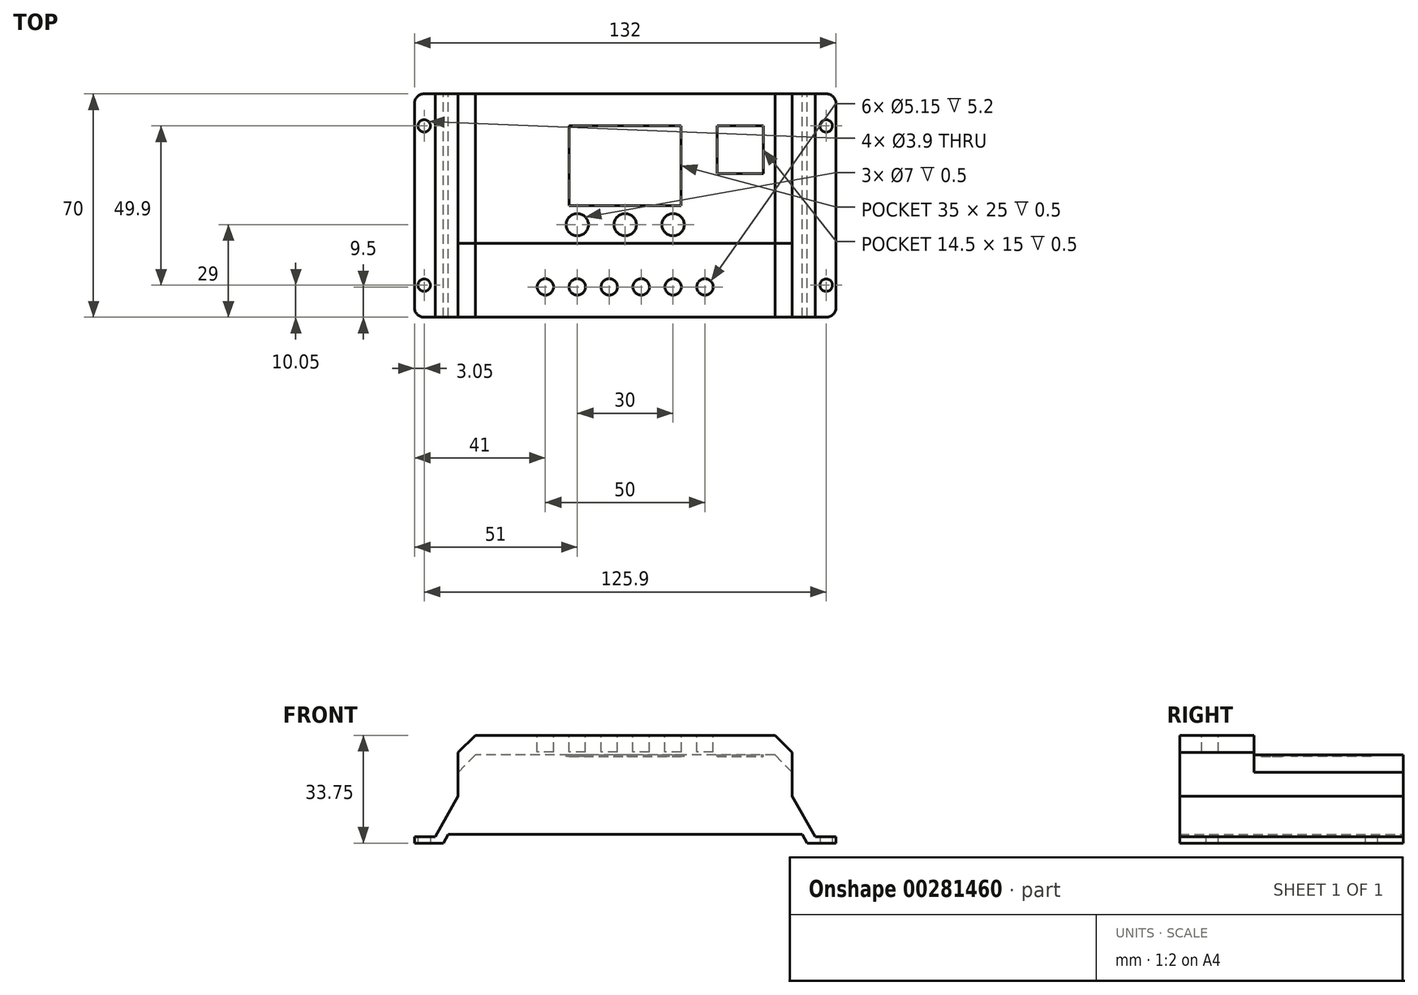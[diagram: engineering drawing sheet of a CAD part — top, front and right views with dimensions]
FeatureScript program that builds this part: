
annotation { "Feature Type Name" : "Feature", "Feature Type Description" : "" }
export const myFeature = defineFeature(function(context is Context, id is Id, definition is map)
    precondition{}
    {
        {
            var Q0;
            Q0=qCreatedBy(makeId("Top.planeOp"),FACE);
            var sketch = newSketch(context, id + "F0", { "sketchPlane" : qUnion([Q0])});
            skLineSegment(sketch, "E0.bottom", {"start": v(-66, 35) * mm, "end": v(66, 35) * mm});
            skLineSegment(sketch, "E0.top", {"start": v(-66, -35) * mm, "end": v(66, -35) * mm});
            skLineSegment(sketch, "E0.left", {"start": v(-66, 35) * mm, "end": v(-66, -35) * mm});
            skLineSegment(sketch, "E0.right", {"start": v(66, 35) * mm, "end": v(66, -35) * mm});
            skPoint(sketch, "E0.middle", {"position": v(0, 0) * mm});
            skSolve(sketch);
        }
        {
            var Q0;
            Q0=makeQuery(id+"F0.imprint","IMPRINT",FACE,{"disambiguationData":[TD([[makeQuery(id+"F0.imprint","IMPRINT",EDGE,{"derivedFrom":sQuery(id+"F0.wireOp",EDGE,"E0.bottom")}),-1.0]])]});
            extrude(context, id + "F1", {"entities" : qUnion([Q0]), "depth" : 2 * mm});
        }
        {
            var Q0;
            Q0=qCreatedBy(makeId("Front.planeOp"),FACE);
            var sketch = newSketch(context, id + "F2", { "sketchPlane" : qUnion([Q0])});
            skLineSegment(sketch, "E1", {"start": v(-59.5, 2) * mm, "end": v(-52.3, 14.7) * mm});
            skLineSegment(sketch, "E2", {"start": v(-52.3, 14.7) * mm, "end": v(-52.3, 22.2) * mm});
            skLineSegment(sketch, "E3", {"start": v(-52.3, 22.2) * mm, "end": v(-46.9, 27.6) * mm});
            skLineSegment(sketch, "E4", {"start": v(-46.9, 27.6) * mm, "end": v(46.9, 27.6) * mm});
            skLineSegment(sketch, "E5", {"start": v(46.9, 27.6) * mm, "end": v(52.3, 22.2) * mm});
            skLineSegment(sketch, "E6", {"start": v(52.3, 22.2) * mm, "end": v(52.3, 14.7) * mm});
            skLineSegment(sketch, "E7", {"start": v(52.3, 14.7) * mm, "end": v(59.5, 2) * mm});
            skLineSegment(sketch, "E8", {"start": v(59.5, 2) * mm, "end": v(-59.5, 2) * mm});
            skLineSegment(sketch, "E9", {"start": v(0, 27.6) * mm, "end": v(0, 0) * mm, "construction": true});
            skSolve(sketch);
        }
        {
            var Q0;
            Q0 = qSketchRegion(id + "F2", true);
            var Q1;
            Q1=makeQuery(id+"F1.opExtrude","SWEPT_FACE",FACE,{"disambiguationData":[OSD([sQuery(id+"F0.wireOp",EDGE,"E0.top")])]});
            extrude(context, id + "F3", {"entities" : qUnion([Q0]), "operationType" : NewBodyOperationType.ADD, "endBound" : BoundingType.UP_TO_SURFACE, "endBoundEntityFace" : qUnion([Q1]), "depth" : 25 * mm});
        }
        {
            var Q0;
            Q0 = qSketchRegion(id + "F2", true);
            var Q1;
            Q1=makeQuery(id+"F1.opExtrude","SWEPT_FACE",FACE,{"disambiguationData":[OSD([sQuery(id+"F0.wireOp",EDGE,"E0.bottom")])]});
            extrude(context, id + "F4", {"entities" : qUnion([Q0]), "operationType" : NewBodyOperationType.ADD, "endBound" : BoundingType.UP_TO_SURFACE, "oppositeDirection" : true, "endBoundEntityFace" : qUnion([Q1]), "depth" : 25 * mm});
        }
        {
            var Q0;
            {var subQ0=sQuery(id+"F0.wireOp",EDGE,"E0.top");Q0=makeQuery(id+"F3.boolean.opBoolean","MERGE",FACE,{"derivedFrom":[makeQuery(id+"F1.opExtrude","SWEPT_FACE",FACE,{"disambiguationData":[OSD([subQ0])]}),makeQuery(id+"F3.opExtrude","CAP_FACE",FACE,{"disambiguationData":[OSD([subQ0])],"isStart":false})]});}
            var sketch = newSketch(context, id + "F5", { "sketchPlane" : qUnion([Q0])});
            skLineSegment(sketch, "E10", {"start": v(-52.3, 22.2) * mm, "end": v(-52.3, 28.35) * mm});
            skLineSegment(sketch, "E11", {"start": v(-52.3, 28.35) * mm, "end": v(-46.9, 33.75) * mm});
            skLineSegment(sketch, "E12", {"start": v(-46.9, 33.75) * mm, "end": v(46.9, 33.75) * mm});
            skLineSegment(sketch, "E13", {"start": v(46.9, 33.75) * mm, "end": v(52.3, 28.35) * mm});
            skLineSegment(sketch, "E14", {"start": v(52.3, 28.35) * mm, "end": v(52.3, 22.2) * mm});
            skLineSegment(sketch, "E15", {"start": v(-46.9, 27.6) * mm, "end": v(-52.3, 22.2) * mm});
            skLineSegment(sketch, "E16", {"start": v(-46.9, 27.6) * mm, "end": v(46.9, 27.6) * mm});
            skLineSegment(sketch, "E17", {"start": v(46.9, 27.6) * mm, "end": v(52.3, 22.2) * mm});
            skSolve(sketch);
        }
        {
            var Q0;
            Q0 = qSketchRegion(id + "F5", true);
            extrude(context, id + "F6", {"entities" : qUnion([Q0]), "operationType" : NewBodyOperationType.ADD, "oppositeDirection" : true, "depth" : 23.2 * mm});
        }
        {
            var Q0;
            Q0=makeQuery(id+"F1.opExtrude","CAP_FACE",FACE,{"disambiguationData":[OSD([sQuery(id+"F0.wireOp",EDGE,"E0.bottom"),sQuery(id+"F0.wireOp",EDGE,"E0.top"),sQuery(id+"F0.wireOp",EDGE,"E0.left"),sQuery(id+"F0.wireOp",EDGE,"E0.right")])],"isStart":true});
            var sketch = newSketch(context, id + "F7", { "sketchPlane" : qUnion([Q0])});
            skCircle(sketch, "E18", {"center": v(62.95, -24.95) * mm, "radius": 1.95 * mm});
            skCircle(sketch, "E19", {"center": v(62.95, 24.95) * mm, "radius": 1.95 * mm});
            skCircle(sketch, "E20", {"center": v(-62.95, 24.95) * mm, "radius": 1.95 * mm});
            skCircle(sketch, "E21", {"center": v(-62.95, -24.95) * mm, "radius": 1.95 * mm});
            skLineSegment(sketch, "E22", {"start": v(62.95, -24.95) * mm, "end": v(62.95, 24.95) * mm, "construction": true});
            skLineSegment(sketch, "E23", {"start": v(-62.95, 24.95) * mm, "end": v(62.95, 24.95) * mm, "construction": true});
            skLineSegment(sketch, "E24", {"start": v(-62.95, -24.95) * mm, "end": v(-62.95, 24.95) * mm, "construction": true});
            skLineSegment(sketch, "E25", {"start": v(62.95, -24.95) * mm, "end": v(-62.95, -24.95) * mm, "construction": true});
            skLineSegment(sketch, "E26", {"start": v(66, 0) * mm, "end": v(62.95, 0) * mm, "construction": true});
            skLineSegment(sketch, "E27", {"start": v(0, -35) * mm, "end": v(0, -24.95) * mm, "construction": true});
            skSolve(sketch);
        }
        {
            var Q0;
            Q0 = qSketchRegion(id + "F7", true);
            extrude(context, id + "F8", {"entities" : qUnion([Q0]), "operationType" : NewBodyOperationType.REMOVE, "oppositeDirection" : true, "depth" : 25 * mm});
        }
        {
            var Q0;
            Q0=makeQuery(id+"F1.opExtrude","SWEPT_EDGE",EDGE,{"disambiguationData":[OSD([sQuery(id+"F0.wireOp",EDGE,"E0.top"),sQuery(id+"F0.wireOp",EDGE,"E0.right")])]});
            var Q1;
            Q1=makeQuery(id+"F1.opExtrude","SWEPT_EDGE",EDGE,{"disambiguationData":[OSD([sQuery(id+"F0.wireOp",EDGE,"E0.bottom"),sQuery(id+"F0.wireOp",EDGE,"E0.right")])]});
            var Q2;
            Q2=makeQuery(id+"F1.opExtrude","SWEPT_EDGE",EDGE,{"disambiguationData":[OSD([sQuery(id+"F0.wireOp",EDGE,"E0.top"),sQuery(id+"F0.wireOp",EDGE,"E0.left")])]});
            var Q3;
            Q3=makeQuery(id+"F1.opExtrude","SWEPT_EDGE",EDGE,{"disambiguationData":[OSD([sQuery(id+"F0.wireOp",EDGE,"E0.bottom"),sQuery(id+"F0.wireOp",EDGE,"E0.left")])]});
            fillet(context, id + "F9", {"entities" : qUnion([Q0, Q1, Q2, Q3]), "radius" : 3 * mm, "tangentPropagation" : true, "allowEdgeOverflow" : false});
        }
        {
            var Q0;
            Q0=makeQuery(id+"F6.opExtrude","SWEPT_FACE",FACE,{"disambiguationData":[OSD([sQuery(id+"F5.wireOp",EDGE,"E12")])]});
            var sketch = newSketch(context, id + "F10", { "sketchPlane" : qUnion([Q0])});
            skCircle(sketch, "E28", {"center": v(-25, -25.5) * mm, "radius": 2.58 * mm});
            skCircle(sketch, "E29", {"center": v(-15, -25.5) * mm, "radius": 2.58 * mm});
            skCircle(sketch, "E30", {"center": v(-5, -25.5) * mm, "radius": 2.58 * mm});
            skCircle(sketch, "E31", {"center": v(5, -25.5) * mm, "radius": 2.58 * mm});
            skCircle(sketch, "E32", {"center": v(15, -25.5) * mm, "radius": 2.58 * mm});
            skCircle(sketch, "E33", {"center": v(25, -25.5) * mm, "radius": 2.58 * mm});
            skLineSegment(sketch, "E34", {"start": v(-25, -25.5) * mm, "end": v(-15, -25.5) * mm, "construction": true});
            skLineSegment(sketch, "E35", {"start": v(-5, -25.5) * mm, "end": v(-15, -25.5) * mm, "construction": true});
            skLineSegment(sketch, "E36", {"start": v(-5, -25.5) * mm, "end": v(5, -25.5) * mm, "construction": true});
            skLineSegment(sketch, "E37", {"start": v(5, -25.5) * mm, "end": v(15, -25.5) * mm, "construction": true});
            skLineSegment(sketch, "E38", {"start": v(15, -25.5) * mm, "end": v(25, -25.5) * mm, "construction": true});
            skLineSegment(sketch, "E39", {"start": v(0, -35) * mm, "end": v(0, -25.5) * mm, "construction": true});
            skSolve(sketch);
        }
        {
            var Q0;
            Q0 = qSketchRegion(id + "F10", true);
            extrude(context, id + "F11", {"entities" : qUnion([Q0]), "operationType" : NewBodyOperationType.REMOVE, "oppositeDirection" : true, "depth" : 5.2 * mm});
        }
        {
            var Q0;
            {var subQ0=sQuery(id+"F0.wireOp",EDGE,"E0.bottom");Q0=makeQuery(id+"F4.boolean.opBoolean","MERGE",FACE,{"derivedFrom":[makeQuery(id+"F1.opExtrude","SWEPT_FACE",FACE,{"disambiguationData":[OSD([subQ0])]}),makeQuery(id+"F4.opExtrude","CAP_FACE",FACE,{"disambiguationData":[OSD([subQ0])],"isStart":false})]});}
            var sketch = newSketch(context, id + "F12", { "sketchPlane" : qUnion([Q0])});
            skLineSegment(sketch, "E40", {"start": v(57, 0) * mm, "end": v(55.41, 2.8) * mm});
            skLineSegment(sketch, "E41", {"start": v(55.41, 2.8) * mm, "end": v(-55.41, 2.8) * mm});
            skLineSegment(sketch, "E42", {"start": v(-55.41, 2.8) * mm, "end": v(-57, 0) * mm});
            skLineSegment(sketch, "E43", {"start": v(-57, 0) * mm, "end": v(57, 0) * mm});
            skLineSegment(sketch, "E44", {"start": v(0, 2.8) * mm, "end": v(0, 27.6) * mm, "construction": true});
            skSolve(sketch);
        }
        {
            var Q0;
            Q0 = qSketchRegion(id + "F12", true);
            extrude(context, id + "F13", {"entities" : qUnion([Q0]), "operationType" : NewBodyOperationType.REMOVE, "endBound" : BoundingType.THROUGH_ALL, "oppositeDirection" : true, "depth" : 25 * mm});
        }
        {
            var Q0;
            {var subQ0=sQuery(id+"F2.wireOp",EDGE,"E4");Q0=makeQuery(id+"F4.boolean.opBoolean","MERGE",FACE,{"derivedFrom":[makeQuery(id+"F3.opExtrude","SWEPT_FACE",FACE,{"disambiguationData":[OSD([subQ0])]}),makeQuery(id+"F4.opExtrude","SWEPT_FACE",FACE,{"disambiguationData":[OSD([subQ0])]})]});}
            var sketch = newSketch(context, id + "F14", { "sketchPlane" : qUnion([Q0])});
            skLineSegment(sketch, "E45.bottom", {"start": v(-17.5, 25) * mm, "end": v(17.5, 25) * mm});
            skLineSegment(sketch, "E45.top", {"start": v(-17.5, 0) * mm, "end": v(17.5, 0) * mm});
            skLineSegment(sketch, "E45.left", {"start": v(-17.5, 25) * mm, "end": v(-17.5, 0) * mm});
            skLineSegment(sketch, "E45.right", {"start": v(17.5, 25) * mm, "end": v(17.5, 0) * mm});
            skPoint(sketch, "E45.middle", {"position": v(0, 12.5) * mm});
            skPoint(sketch, "E45.middle.positionSnap0", {"position": v(0, 35) * mm});
            skPoint(sketch, "E45.centerSnap0", {"position": v(0, 35) * mm});
            skCircle(sketch, "E46", {"center": v(0, -6) * mm, "radius": 3.5 * mm});
            skPoint(sketch, "E46.centerSnap0", {"position": v(0, 0) * mm});
            skCircle(sketch, "E47", {"center": v(-15, -6) * mm, "radius": 3.5 * mm});
            skCircle(sketch, "E48", {"center": v(15, -6) * mm, "radius": 3.5 * mm});
            skLineSegment(sketch, "E49", {"start": v(-15, -6) * mm, "end": v(0, -6) * mm, "construction": true});
            skLineSegment(sketch, "E50", {"start": v(15, -6) * mm, "end": v(0, -6) * mm, "construction": true});
            skLineSegment(sketch, "E51.bottom", {"start": v(28.75, 25) * mm, "end": v(43.25, 25) * mm});
            skLineSegment(sketch, "E51.top", {"start": v(28.75, 10) * mm, "end": v(43.25, 10) * mm});
            skLineSegment(sketch, "E51.left", {"start": v(28.75, 25) * mm, "end": v(28.75, 10) * mm});
            skLineSegment(sketch, "E51.right", {"start": v(43.25, 25) * mm, "end": v(43.25, 10) * mm});
            skPoint(sketch, "E51.middle", {"position": v(36, 17.5) * mm});
            skLineSegment(sketch, "E52", {"start": v(17.5, 25) * mm, "end": v(28.75, 25) * mm, "construction": true});
            skSolve(sketch);
        }
        {
            var Q0;
            Q0 = qSketchRegion(id + "F14", true);
            extrude(context, id + "F15", {"entities" : qUnion([Q0]), "operationType" : NewBodyOperationType.REMOVE, "oppositeDirection" : true, "depth" : .5 * mm});
        }
    });
